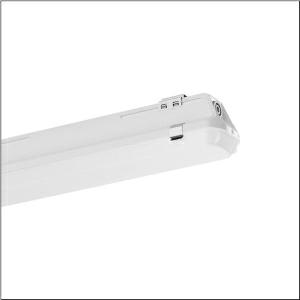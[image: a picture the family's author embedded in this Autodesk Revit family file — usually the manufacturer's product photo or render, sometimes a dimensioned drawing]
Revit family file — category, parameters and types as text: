
# Revit family: monsun_r__21_emergency_51fb107p487b3g_e760
name_source: partatom
category: Lighting Fixtures
units: mm (PartAtom-declared; Revit-internal decimal feet)

## family parameters
Cut with Voids When Loaded = No
Host = Face
Light Source = No
Part Type = Normal
Room Calculation Point = No
Round Connector Dimension = Use Diameter
Shared = No

## types (1)
- Monsun® 21 emergency (1 x LED, 8090 lm, 57.3 W, 4000K)
    Apparent Load = 57 VA
    CIE Flux Codes = 47 77 93 94 100
    Color Rendering = 80
    Color Temperature = 4000K
    Default Elevation = 1800 mm
    Description = Monsun® 21 emergency, damp-proof luminaire, chain hanger, primary optical cover: enclosure, of PMMA, light emission: direct distribution, primary light characteristic: symmetric, installation type: vertical mounting, horizontal mounting, surface-mounted, suspended mounting, LED, rated luminous flux: 8.090lm, luminous efficacy: 141lm/W, light colour: 840, colour temperature: 4000K, control gear: ECG, with terminal, 4-pole, max. 2.5mm², mains connection: 220..240V, AC, 50/60Hz, rated input power: 57W, control gear: single battery element, battery: NiCd, 4,5Ah, mains connection: 230V, housing, of glass-fibre reinforced polyester, uncoated, bright grey, incl. chain hanger, length: 1.590mm, width: 90mm, height: 88mm, clip for enclosure, of stainless steel (V2A), ceiling mounting element, of stainless steel (V2A), chain hanger, of stainless steel (V2A), protection rating (complete): IP66, insulation class (complete): insulation class I (protective earthing), certification: CE, UKCA, protection symbol: D, impact resistance: IK04, permissible operating ambient temperature: +5..+25°C, standard: EN 60598-2-1, EN 50419, EN 60598-2-22, corresponds to IFS (International Featured Standards) requirements for safety and quality in the food industry, for indoor or canopied outdoor use, no direct snow, no direct sun, no direct rain, contact your sales advisor before using the luminaires in applications with unclear chemical exposure, large temperature fluctuations or condensation-forming humidity, LABS conformity tested according to VDMA 24364:2018-05, packaging unit: 1 piece
    Height = 89 mm
    Lamp = 1 x LED
    Lamp Light Flux = 8090 lm
    Lamp Power = 57.3 W
    Lamp count = 1
    Length = 1590 mm
    Luminous efficacy = 141 lm/W
    Manufacturer = Siteco
    ModVariant = No
    Model = 51FB107P487B3G
    Mounting Place = Ceiling
    Mounting Type = Surface mounted
    Number of Poles = 1
    OnlyDefault = Yes
    Power Factor = 1
    Product Name = Monsun® 21 emergency
    Product group = damp-proof luminaire
    ProductGroupID = 301
    Protection Class = Protection class I
    Protection Degree = IP 66
    RLX_Detail_Level = 1
    RLX_Emergency_Light_Flux = 0 lm
    RLX_Emergency_Type = 0
    RLX_Emergency_Type_DB = No
    RlxData = <blob elided: 89037 chars, md5=ab0ae6a8>
    Socket = socket
    Standby Power = 0 W
    System Light Flux = 8090 lm
    System Power = 57 W
    Type Comments = Product without accessories
    Type Image = l_1006717.jpg
    URL = http://relux.com
    VarID = ---
    Voltage = 0 V
    Weight = 0.00 kg
    Width = 90 mm

## geometry (parser evidence)
native form markers: Blend x4, Sweep x12
no freeform markers — native parametric forms only
